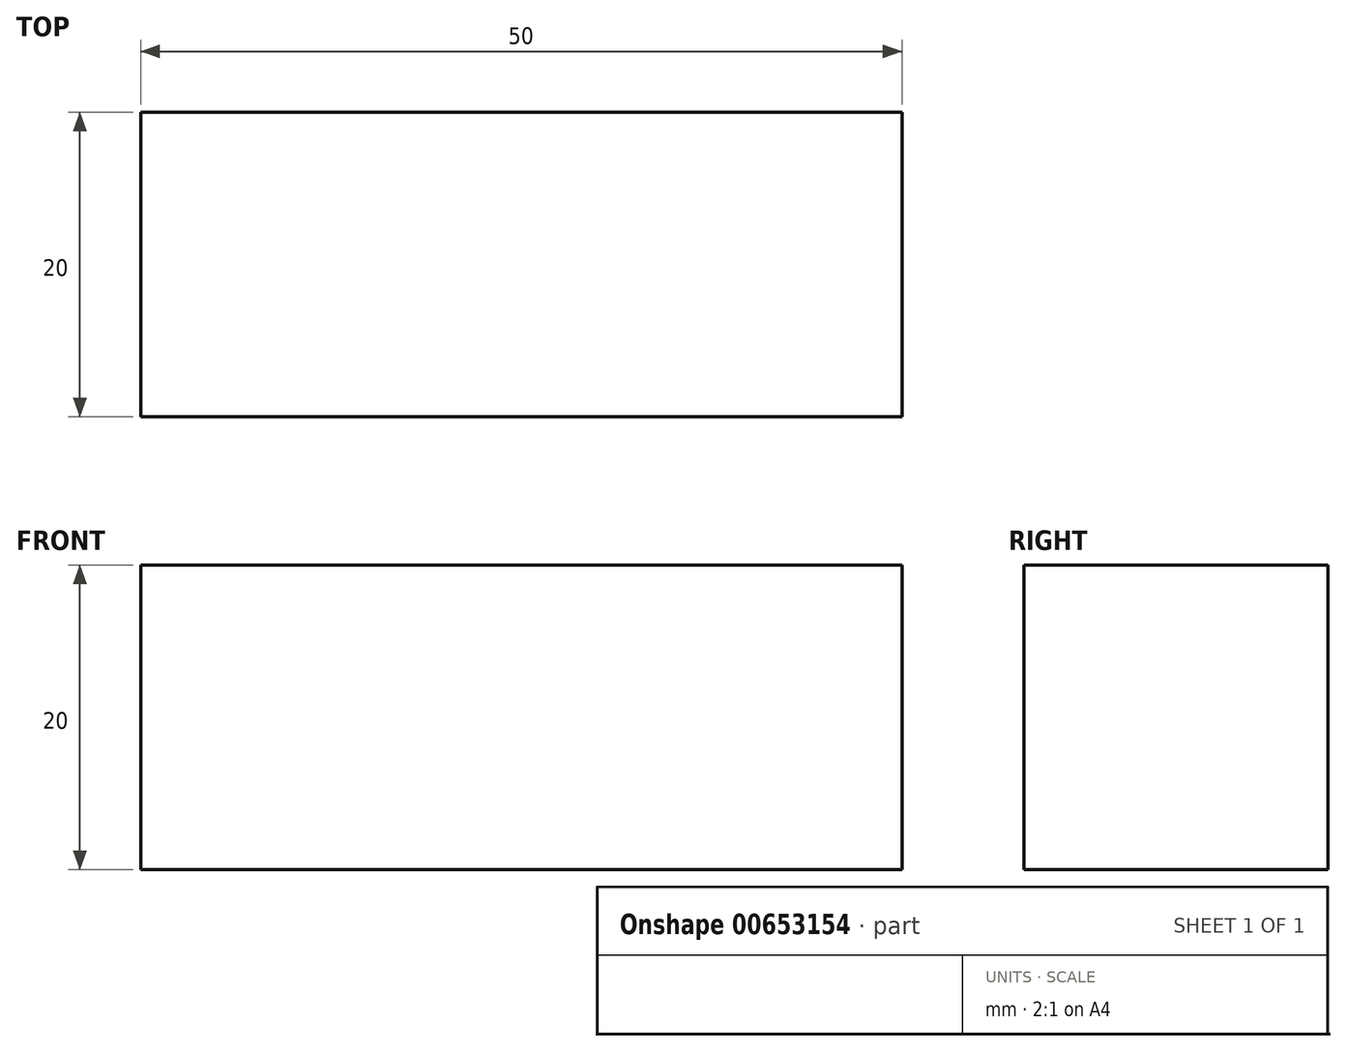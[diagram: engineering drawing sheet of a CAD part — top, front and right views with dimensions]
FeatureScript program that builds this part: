
annotation { "Feature Type Name" : "Feature", "Feature Type Description" : "" }
export const myFeature = defineFeature(function(context is Context, id is Id, definition is map)
    precondition{}
    {
        {
            var Q0;
            Q0=qCreatedBy(makeId("Front.planeOp"),FACE);
            var sketch = newSketch(context, id + "F0", { "sketchPlane" : qUnion([Q0])});
            skLineSegment(sketch, "E0.bottom", {"start": v(25, -10) * mm, "end": v(-25, -10) * mm});
            skLineSegment(sketch, "E0.top", {"start": v(25, 10) * mm, "end": v(-25, 10) * mm});
            skLineSegment(sketch, "E0.left", {"start": v(25, -10) * mm, "end": v(25, 10) * mm});
            skLineSegment(sketch, "E0.right", {"start": v(-25, -10) * mm, "end": v(-25, 10) * mm});
            skPoint(sketch, "E0.middle", {"position": v(0, 0) * mm});
            skSolve(sketch);
        }
        {
            var Q0;
            Q0 = qSketchRegion(id + "F0", true);
            extrude(context, id + "F1", {"entities" : qUnion([Q0]), "depth" : 20 * mm, "offsetDistance" : 25 * mm});
        }
    });
